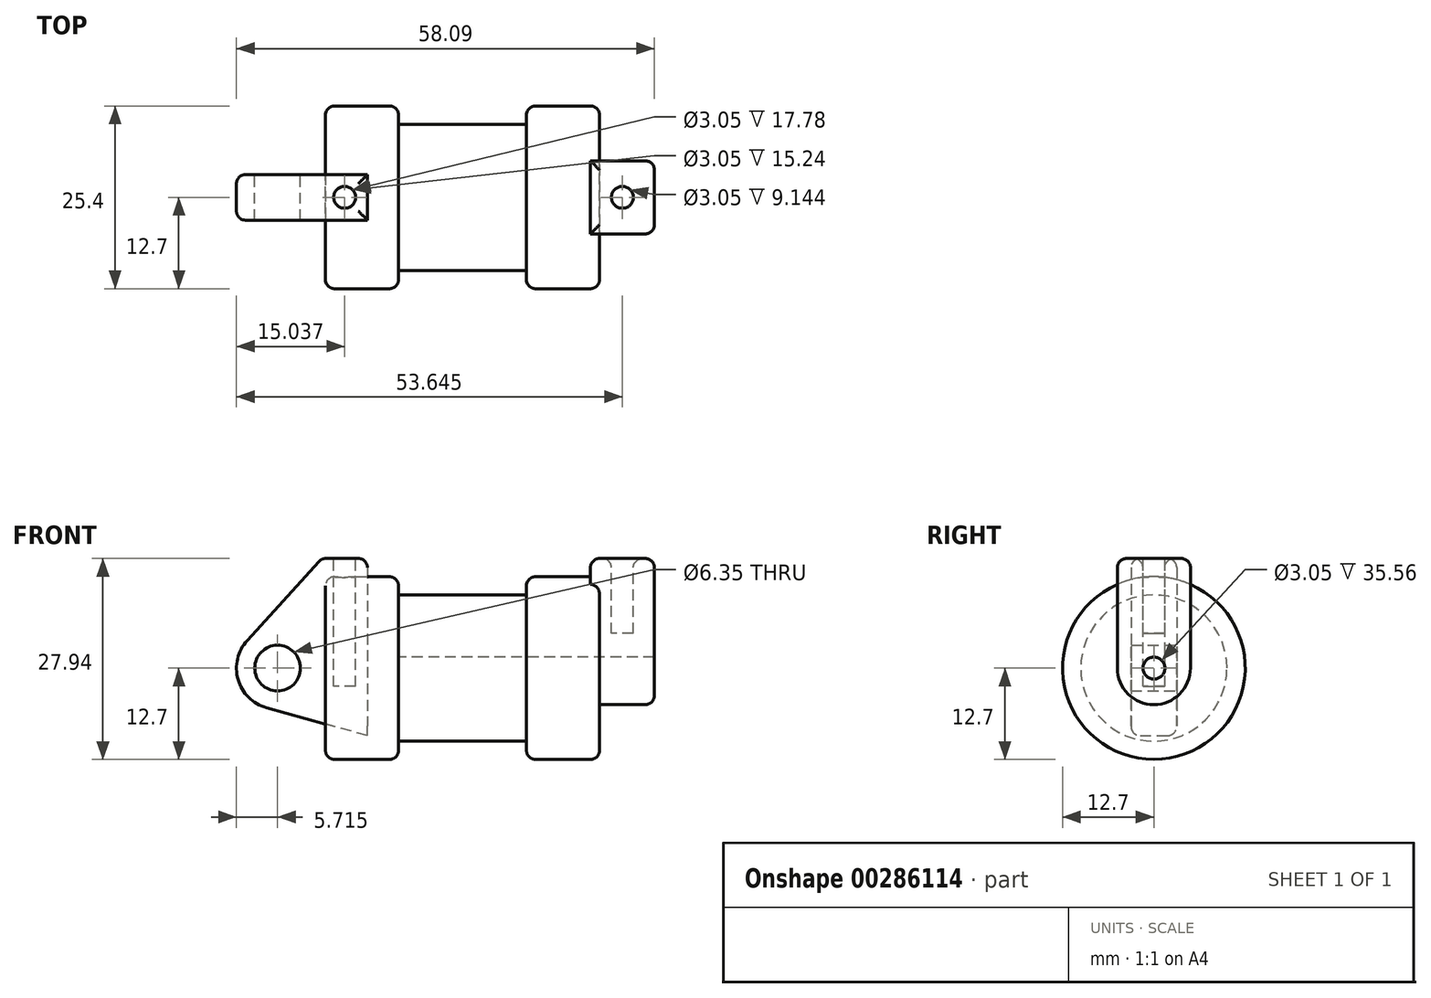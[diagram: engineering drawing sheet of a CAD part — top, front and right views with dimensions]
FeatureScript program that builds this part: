
annotation { "Feature Type Name" : "Feature", "Feature Type Description" : "" }
export const myFeature = defineFeature(function(context is Context, id is Id, definition is map)
    precondition{}
    {
        {
            var Q0;
            Q0=qCreatedBy(makeId("Front.planeOp"),FACE);
            var sketch = newSketch(context, id + "F0", { "sketchPlane" : qUnion([Q0])});
            skLineSegment(sketch, "E0", {"start": v(0, 0) * mm, "end": v(0, 12.7) * mm});
            skLineSegment(sketch, "E1", {"start": v(0, 12.7) * mm, "end": v(10.16, 12.7) * mm});
            skLineSegment(sketch, "E2", {"start": v(10.16, 12.7) * mm, "end": v(10.16, 10.16) * mm});
            skLineSegment(sketch, "E3", {"start": v(10.16, 10.16) * mm, "end": v(27.94, 10.16) * mm});
            skLineSegment(sketch, "E4", {"start": v(27.94, 10.16) * mm, "end": v(27.94, 12.7) * mm});
            skLineSegment(sketch, "E5", {"start": v(27.94, 12.7) * mm, "end": v(38.1, 12.7) * mm});
            skLineSegment(sketch, "E6", {"start": v(38.1, 12.7) * mm, "end": v(38.1, 0) * mm});
            skLineSegment(sketch, "E7", {"start": v(38.1, 0) * mm, "end": v(0, 0) * mm});
            skLineSegment(sketch, "E8", {"start": v(5.84, 15.24) * mm, "end": v(-0.5, 15.24) * mm});
            skLineSegment(sketch, "E9", {"start": v(-0.5, 15.24) * mm, "end": v(-10.88, 3.85) * mm});
            skLineSegment(sketch, "E10", {"start": v(0, 0) * mm, "end": v(-6.65, 0) * mm});
            skCircle(sketch, "E11", {"center": v(-6.65, 0) * mm, "radius": 5.72 * mm});
            skCircle(sketch, "E12", {"center": v(-6.65, 0) * mm, "radius": 3.18 * mm});
            skLineSegment(sketch, "E13", {"start": v(5.84, 15.24) * mm, "end": v(5.84, -9.4) * mm});
            skLineSegment(sketch, "E14", {"start": v(5.84, -9.4) * mm, "end": v(-8.18, -5.5) * mm});
            skSolve(sketch);
        }
        {
            var Q0;
            {var subQ0=sQuery(id+"F0.wireOp",EDGE,"E2");Q0=makeQuery(id+"F0.imprint","IMPRINT",FACE,{"disambiguationData":[TD([[makeQuery(id+"F0.imprint","IMPRINT",EDGE,{"derivedFrom":subQ0}),-1.0]])]});}
            var Q1;
            {var subQ0=sQuery(id+"F0.wireOp",EDGE,"E0");Q1=makeQuery(id+"F0.imprint","IMPRINT",FACE,{"disambiguationData":[TD([[makeQuery(id+"F0.imprint","IMPRINT",EDGE,{"derivedFrom":subQ0}),-1.0]])]});}
            var Q2;
            Q2=sQuery(id+"F0.wireOp",EDGE,"E7");
            revolve(context, id + "F1", {"entities" : qUnion([Q0, Q1]), "axis" : qUnion([Q2]), "revolveType" : RevolveType.FULL});
        }
        {
            var Q0;
            {var subQ0=sQuery(id+"F0.wireOp",EDGE,"E0");Q0=makeQuery(id+"F0.imprint","IMPRINT",FACE,{"disambiguationData":[TD([[makeQuery(id+"F0.imprint","IMPRINT",EDGE,{"derivedFrom":subQ0}),-1.0]])]});}
            var Q1;
            {var subQ1=sQuery(id+"F0.wireOp",EDGE,"E0");Q1=makeQuery(id+"F0.imprint","IMPRINT",FACE,{"disambiguationData":[TD([[makeQuery(id+"F0.imprint","IMPRINT",EDGE,{"derivedFrom":subQ1}),1.0]])]});}
            var Q2;
            {var subQ5=sQuery(id+"F0.wireOp",EDGE,"E12");Q2=makeQuery(id+"F0.imprint","IMPRINT",FACE,{"disambiguationData":[TD([[makeQuery(id+"F0.imprint","IMPRINT",EDGE,{"derivedFrom":subQ5}),-1.0]])]});}
            var Q3;
            {var subQ0=sQuery(id+"F0.wireOp",EDGE,"E14");Q3=makeQuery(id+"F0.imprint","IMPRINT",FACE,{"disambiguationData":[TD([[makeQuery(id+"F0.imprint","IMPRINT",EDGE,{"derivedFrom":subQ0}),-1.0]])]});}
            extrude(context, id + "F2", {"entities" : qUnion([Q0, Q1, Q2, Q3]), "endBound" : BoundingType.SYMMETRIC, "depth" : 6.35 * mm});
        }
        {
            var Q0;
            Q0=makeQuery(id+"F1.opRevolve","SWEPT_FACE",FACE,{"disambiguationData":[OSD([sQuery(id+"F0.wireOp",EDGE,"E6")])]});
            var sketch = newSketch(context, id + "F3", { "sketchPlane" : qUnion([Q0])});
            skCircle(sketch, "E15", {"center": v(0, 0) * mm, "radius": 5.08 * mm});
            skCircle(sketch, "E16", {"center": v(0, 0) * mm, "radius": 1.52 * mm});
            skLineSegment(sketch, "E17.0", {"start": v(-3.18, 15.24) * mm, "end": v(3.17, 15.24) * mm});
            skPoint(sketch, "E18.endSnap0", {"position": v(0, 15.24) * mm});
            skLineSegment(sketch, "E19", {"start": v(-5.08, 15.24) * mm, "end": v(-5.08, 0) * mm});
            skLineSegment(sketch, "E20", {"start": v(5.08, 15.24) * mm, "end": v(5.08, 0) * mm});
            skLineSegment(sketch, "E21", {"start": v(-5.08, 15.24) * mm, "end": v(5.08, 15.24) * mm});
            skSolve(sketch);
        }
        {
            var Q0;
            {var subQ0=sQuery(id+"F3.wireOp",EDGE,"E19");var subQ1=sQuery(id+"F3.wireOp",EDGE,"E15");var subQ2=makeQuery(id+"F3.imprint","INTERSECT",VERTEX,{"derivedFrom":[subQ1,subQ0]});Q0=makeQuery(id+"F3.imprint","IMPRINT",FACE,{"disambiguationData":[TD([[makeQuery(id+"F3.imprint","IMPRINT",EDGE,{"disambiguationData":[TD([[subQ2,1.0]])],"derivedFrom":subQ1}),-1.0]])]});}
            var Q1;
            {var subQ0=sQuery(id+"F3.wireOp",EDGE,"E21");var subQ1=sQuery(id+"F3.wireOp",EDGE,"E19");var subQ2=makeQuery(id+"F3.imprint","INTERSECT",VERTEX,{"derivedFrom":[subQ1,subQ0]});Q1=makeQuery(id+"F3.imprint","IMPRINT",FACE,{"disambiguationData":[TD([[makeQuery(id+"F3.imprint","IMPRINT",EDGE,{"disambiguationData":[TD([[subQ2,-1.0]])],"derivedFrom":subQ0}),-1.0]])]});}
            var Q2;
            Q2=makeQuery(id+"F3.imprint","IMPRINT",FACE,{"disambiguationData":[TD([[makeQuery(id+"F3.imprint","IMPRINT",EDGE,{"derivedFrom":sQuery(id+"F3.wireOp",EDGE,"E16")}),-1.0]])]});
            extrude(context, id + "F4", {"entities" : qUnion([Q0, Q1, Q2]), "operationType" : NewBodyOperationType.ADD, "oppositeDirection" : true, "depth" : 1.27 * mm});
        }
        {
            var Q0;
            Q0=makeQuery(id+"F3.imprint","IMPRINT",FACE,{"disambiguationData":[TD([[makeQuery(id+"F3.imprint","IMPRINT",EDGE,{"derivedFrom":sQuery(id+"F3.wireOp",EDGE,"E16")}),-1.0]])]});
            var Q1;
            {var subQ0=sQuery(id+"F3.wireOp",EDGE,"E19");var subQ1=sQuery(id+"F3.wireOp",EDGE,"E15");var subQ2=makeQuery(id+"F3.imprint","INTERSECT",VERTEX,{"derivedFrom":[subQ1,subQ0]});Q1=makeQuery(id+"F3.imprint","IMPRINT",FACE,{"disambiguationData":[TD([[makeQuery(id+"F3.imprint","IMPRINT",EDGE,{"disambiguationData":[TD([[subQ2,1.0]])],"derivedFrom":subQ1}),-1.0]])]});}
            var Q2;
            {var subQ0=sQuery(id+"F3.wireOp",EDGE,"E21");var subQ1=sQuery(id+"F3.wireOp",EDGE,"E19");var subQ2=makeQuery(id+"F3.imprint","INTERSECT",VERTEX,{"derivedFrom":[subQ1,subQ0]});Q2=makeQuery(id+"F3.imprint","IMPRINT",FACE,{"disambiguationData":[TD([[makeQuery(id+"F3.imprint","IMPRINT",EDGE,{"disambiguationData":[TD([[subQ2,-1.0]])],"derivedFrom":subQ0}),-1.0]])]});}
            extrude(context, id + "F5", {"entities" : qUnion([Q0, Q1, Q2]), "operationType" : NewBodyOperationType.ADD, "depth" : 7.62 * mm});
        }
        {
            var Q0;
            Q0=makeQuery(id+"F3.imprint","IMPRINT",FACE,{"disambiguationData":[TD([[makeQuery(id+"F3.imprint","IMPRINT",EDGE,{"derivedFrom":sQuery(id+"F3.wireOp",EDGE,"E16")}),1.0]])]});
            var Q1;
            Q1=makeQuery(id+"F1.opRevolve","SWEPT_FACE",FACE,{"disambiguationData":[OSD([sQuery(id+"F0.wireOp",EDGE,"E2")])]});
            extrude(context, id + "F6", {"entities" : qUnion([Q0]), "operationType" : NewBodyOperationType.REMOVE, "endBound" : BoundingType.UP_TO_SURFACE, "oppositeDirection" : true, "endBoundEntityFace" : qUnion([Q1]), "depth" : 25.4 * mm});
        }
        {
            var Q0;
            Q0=makeQuery(id+"F2.opExtrude","SWEPT_FACE",FACE,{"disambiguationData":[OSD([sQuery(id+"F0.wireOp",EDGE,"E8")])]});
            var sketch = newSketch(context, id + "F7", { "sketchPlane" : qUnion([Q0])});
            skLineSegment(sketch, "E22.0.0", {"start": v(5.84, 3.18) * mm, "end": v(-0.5, 3.18) * mm});
            skLineSegment(sketch, "E22.0.1", {"start": v(-0.5, 3.17) * mm, "end": v(-0.5, -3.18) * mm});
            skLineSegment(sketch, "E22.0.2", {"start": v(-0.5, -3.18) * mm, "end": v(5.84, -3.18) * mm});
            skLineSegment(sketch, "E22.0.3", {"start": v(5.84, -3.18) * mm, "end": v(5.84, 3.17) * mm});
            skLineSegment(sketch, "E23.0.0", {"start": v(36.83, -5.08) * mm, "end": v(45.72, -5.08) * mm});
            skLineSegment(sketch, "E23.0.1", {"start": v(45.72, -5.08) * mm, "end": v(45.72, 5.08) * mm});
            skLineSegment(sketch, "E23.0.2", {"start": v(45.72, 5.08) * mm, "end": v(36.83, 5.08) * mm});
            skLineSegment(sketch, "E23.0.3", {"start": v(36.83, 5.08) * mm, "end": v(36.83, -5.08) * mm});
            skCircle(sketch, "E24", {"center": v(2.67, 0) * mm, "radius": 1.52 * mm});
            skPoint(sketch, "E24.centerSnap0", {"position": v(-0.5, 0) * mm});
            skPoint(sketch, "E24.centerSnap1", {"position": v(2.67, -3.18) * mm});
            skCircle(sketch, "E25", {"center": v(41.28, 0) * mm, "radius": 1.52 * mm});
            skPoint(sketch, "E25.centerSnap0", {"position": v(36.83, 0) * mm});
            skPoint(sketch, "E25.centerSnap1", {"position": v(41.28, 5.08) * mm});
            skSolve(sketch);
        }
        {
            var Q0;
            Q0=makeQuery(id+"F7.imprint","IMPRINT",FACE,{"disambiguationData":[TD([[makeQuery(id+"F7.imprint","IMPRINT",EDGE,{"derivedFrom":sQuery(id+"F7.wireOp",EDGE,"E24")}),1.0]])]});
            extrude(context, id + "F8", {"entities" : qUnion([Q0]), "operationType" : NewBodyOperationType.REMOVE, "oppositeDirection" : true, "depth" : 17.78 * mm});
        }
        {
            var Q0;
            Q0=makeQuery(id+"F7.imprint","IMPRINT",FACE,{"disambiguationData":[TD([[makeQuery(id+"F7.imprint","IMPRINT",EDGE,{"derivedFrom":sQuery(id+"F7.wireOp",EDGE,"E25")}),1.0]])]});
            extrude(context, id + "F9", {"entities" : qUnion([Q0]), "operationType" : NewBodyOperationType.REMOVE, "oppositeDirection" : true, "depth" : 10.4 * mm});
        }
        {
            var Q0;
            Q0=makeQuery(id+"F2.opExtrude","CAP_EDGE",EDGE,{"disambiguationData":[OSD([sQuery(id+"F0.wireOp",EDGE,"E8")])],"isStart":false});
            var Q1;
            Q1=makeQuery(id+"F2.opExtrude","SWEPT_EDGE",EDGE,{"disambiguationData":[OSD([sQuery(id+"F0.wireOp",EDGE,"E8"),sQuery(id+"F0.wireOp",EDGE,"E13")])]});
            var Q2;
            Q2=makeQuery(id+"F2.opExtrude","CAP_EDGE",EDGE,{"disambiguationData":[OSD([sQuery(id+"F0.wireOp",EDGE,"E8")])],"isStart":true});
            var Q3;
            Q3=makeQuery(id+"F2.opExtrude","SWEPT_EDGE",EDGE,{"disambiguationData":[OSD([sQuery(id+"F0.wireOp",EDGE,"E8"),sQuery(id+"F0.wireOp",EDGE,"E9")])]});
            var Q4;
            Q4=makeQuery(id+"F1.opRevolve","SWEPT_EDGE",EDGE,{"disambiguationData":[OSD([sQuery(id+"F0.wireOp",EDGE,"E1"),sQuery(id+"F0.wireOp",EDGE,"E2")])]});
            var Q5;
            Q5=makeQuery(id+"F1.opRevolve","SWEPT_EDGE",EDGE,{"disambiguationData":[OSD([sQuery(id+"F0.wireOp",EDGE,"E0"),sQuery(id+"F0.wireOp",EDGE,"E1")])]});
            var Q6;
            Q6=makeQuery(id+"F2.opExtrude","CAP_EDGE",EDGE,{"disambiguationData":[OSD([sQuery(id+"F0.wireOp",EDGE,"E9")])],"isStart":false});
            var Q7;
            Q7=makeQuery(id+"F2.opExtrude","CAP_EDGE",EDGE,{"disambiguationData":[OSD([sQuery(id+"F0.wireOp",EDGE,"E11")])],"isStart":true});
            var Q8;
            Q8=makeQuery(id+"F1.opRevolve","SWEPT_EDGE",EDGE,{"disambiguationData":[OSD([sQuery(id+"F0.wireOp",EDGE,"E4"),sQuery(id+"F0.wireOp",EDGE,"E5")])]});
            var Q9;
            Q9=makeQuery(id+"F1.opRevolve","SWEPT_EDGE",EDGE,{"disambiguationData":[OSD([sQuery(id+"F0.wireOp",EDGE,"E5"),sQuery(id+"F0.wireOp",EDGE,"E6")])]});
            var Q10;
            Q10=makeQuery(id+"F5.opExtrude","CAP_EDGE",EDGE,{"disambiguationData":[OSD([sQuery(id+"F3.wireOp",EDGE,"E15")])],"isStart":false});
            var Q11;
            {var subQ0=sQuery(id+"F3.wireOp",EDGE,"E21");var subQ1=sQuery(id+"F3.wireOp",EDGE,"E19");Q11=makeQuery(id+"F5.boolean.opBoolean","MERGE",EDGE,{"derivedFrom":[makeQuery(id+"F4.opExtrude","SWEPT_EDGE",EDGE,{"disambiguationData":[OSD([subQ1,subQ0])]}),makeQuery(id+"F5.opExtrude","SWEPT_EDGE",EDGE,{"disambiguationData":[OSD([subQ1,subQ0])]})]});}
            var Q12;
            Q12=makeQuery(id+"F5.opExtrude","CAP_EDGE",EDGE,{"disambiguationData":[OSD([sQuery(id+"F3.wireOp",EDGE,"E21")])],"isStart":false});
            var Q13;
            {var subQ0=sQuery(id+"F3.wireOp",EDGE,"E21");var subQ1=sQuery(id+"F3.wireOp",EDGE,"E20");Q13=makeQuery(id+"F5.boolean.opBoolean","MERGE",EDGE,{"derivedFrom":[makeQuery(id+"F4.opExtrude","SWEPT_EDGE",EDGE,{"disambiguationData":[OSD([subQ1,subQ0])]}),makeQuery(id+"F5.opExtrude","SWEPT_EDGE",EDGE,{"disambiguationData":[OSD([subQ1,subQ0])]})]});}
            var Q14;
            {var subQ0=sQuery(id+"F3.wireOp",EDGE,"E21");Q14=makeQuery(id+"F5.boolean.opBoolean","MERGE",FACE,{"derivedFrom":[makeQuery(id+"F4.opExtrude","SWEPT_FACE",FACE,{"disambiguationData":[OSD([subQ0])]}),makeQuery(id+"F5.opExtrude","SWEPT_FACE",FACE,{"disambiguationData":[OSD([subQ0])]})]});}
            fillet(context, id + "F10", {"entities" : qUnion([Q0, Q1, Q2, Q3, Q4, Q5, Q6, Q7, Q8, Q9, Q10, Q11, Q12, Q13, Q14]), "radius" : 1.27 * mm, "tangentPropagation" : true, "allowEdgeOverflow" : false});
        }
    });
